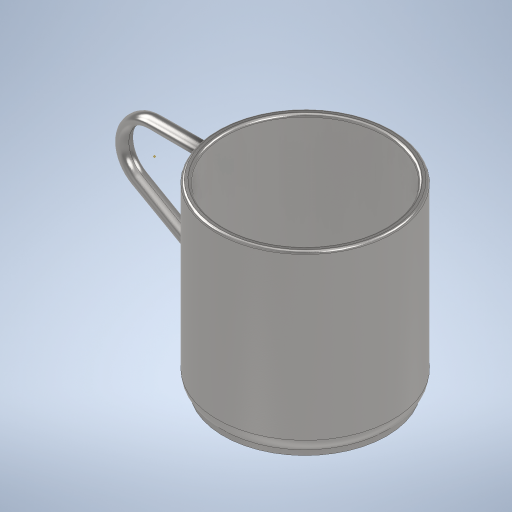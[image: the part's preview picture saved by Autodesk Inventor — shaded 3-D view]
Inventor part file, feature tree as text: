
AUTODESK INVENTOR PART (.ipt)
format: ipt  version: 2024 (Build 280153000, 153)  size: 365,568 bytes
history: native  units: in
note: dims shown in document units (in); Inventor stores cm internally (conversion verified against a paired STEP export)
features: sketch x5, plane x2, revolve x1, shell x1, other x1, loft x1, fillet x1, extrude x1
ambient origin geometry x8: Origin, YZ Plane, XZ Plane, XY Plane, X Axis, Y Axis, Z Axis, Center Point
bodies: Solid1 (feature_tree)
feature tree (13):
  revolve  "Revolution1"  [1 undecoded]
  shell  "Shell1"  Thickness=90.0deg
  sketch  "Sketch3"  dims[d3=2.5591in d4=1.2795in d5=90.0deg]
  other  "Work Point1"
  plane  "Work Plane1"
  sketch  "Sketch4"  dims[d6=0.1181in d7=0.3937in]
  plane  "Work Plane2"
  loft  "Loft1"
  fillet  "Fillet1"  [1 undecoded]
  extrude  "Extrusion1"  Depth=0.3937in
  sketch  "Sketch2"  dims[d0=2.7559in d1=1.378in d2=90.0deg]
  sketch  "Sketch5"  dims[d8=0.5906in]
  sketch  "Sketch6"  dims[d11=0.3937in d13=0.0787in d15=0.1181in d16=0.5906in d17=0.1181in d18=0.0787in d19=0.0in d20=90.0deg d21=0.0in d22=90.0deg d23=0.0in d24=90.0deg d25=0.0394in d26=2.4409in d27=2.5591in d28=0.0787in d29=0.0in]
note: 2 required parameter values undecoded (feature->parameter linkage not recoverable at this tier; creation-order binding heuristic only, values carry confidence <= 0.55)